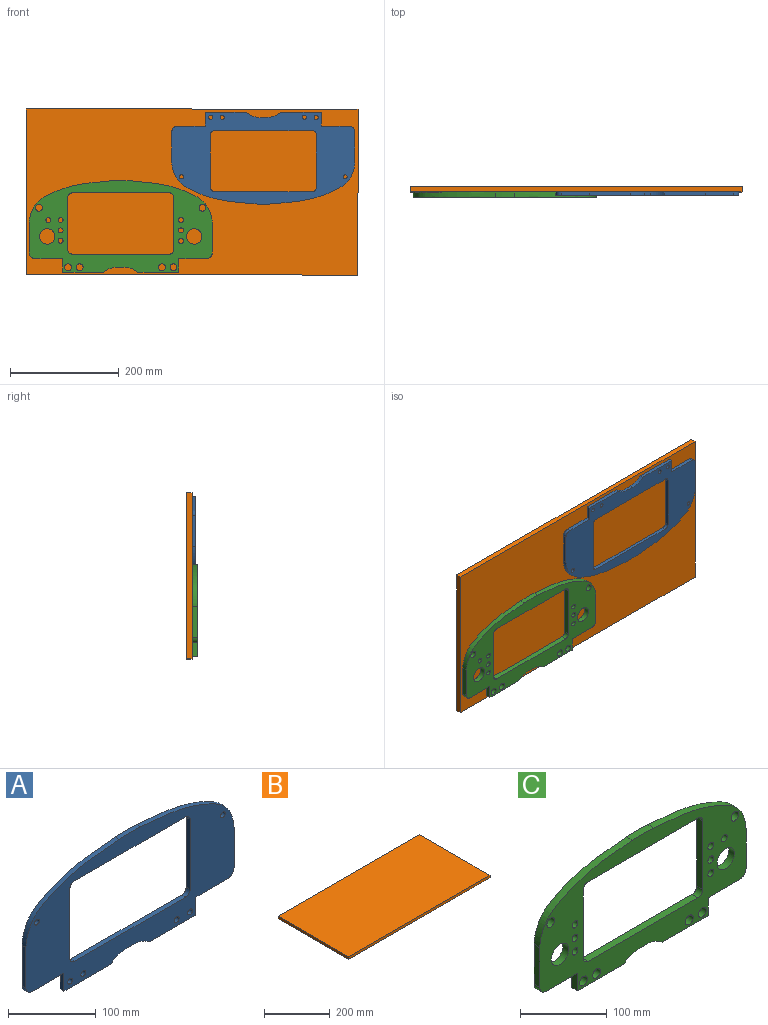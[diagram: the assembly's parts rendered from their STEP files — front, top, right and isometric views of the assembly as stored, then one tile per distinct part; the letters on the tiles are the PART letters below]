
ASSEMBLY  parts=3 mates=3
PART A: 32 faces, bbox 335.9x6.4x168.6 mm
  f0: plane 335.91x168.65mm, normal (0,-1,0), area 25989.5mm2, adj f2,f3,f4,f5,f6,f7,f8,f9
  f1: plane 335.91x168.65mm, normal (0,1,0), area 25989.5mm2, adj f2,f3,f4,f5,f6,f7,f8,f9
  f2: plane 11.66x6.35mm, normal (0,0,-1), area 74.1mm2, adj f0,f1,f3,f20
  f3: cylinder r=39.17mm len=25.6mm, axis (0,1,0), area 177.1mm2, adj f0,f1,f2,f4
  f4: plane 75.09x6.35mm, normal (0,0,-1), area 476.8mm2, adj f0,f1,f3,f5
  f5: plane 25.17x6.35mm, normal (1,0,0), area 159.8mm2, adj f0,f1,f4,f6
  f6: plane 51.28x6.35mm, normal (0,0,-1), area 325.6mm2, adj f0,f1,f5,f21
  f7: plane 56.4x6.35mm, normal (1,0,0), area 358.1mm2, adj f0,f1,f8,f21
  f8: extruded ~150.69x76.24mm, area 1171.7mm2, adj f0,f1,f7,f31
  f9: extruded ~150.69x76.24mm, area 1171.7mm2, adj f0,f1,f10,f31
  f10: plane 56.4x6.35mm, normal (-1,0,0), area 358.1mm2, adj f0,f1,f9,f22
  f11: plane 51.28x6.35mm, normal (0,0,-1), area 325.6mm2, adj f0,f1,f12,f22
  f12: plane 25.17x6.35mm, normal (-1,0,0), area 159.8mm2, adj f0,f1,f11,f13
  f13: plane 75.09x6.35mm, normal (0,0,-1), area 476.8mm2, adj f0,f1,f12,f20
  f14: cylinder r=3.81mm len=7.62mm, axis (0,1,0), area 152mm2, adj f0,f1
  f15: cylinder r=3.81mm len=7.62mm, axis (0,1,0), area 152mm2, adj f0,f1
  f16: cylinder r=3.81mm len=7.62mm, axis (0,1,0), area 152mm2, adj f0,f1
  f17: cylinder r=3.81mm len=7.62mm, axis (0,1,0), area 152mm2, adj f0,f1
  f18: cylinder r=3.81mm len=7.62mm, axis (0,1,0), area 152mm2, adj f0,f1
  f19: cylinder r=3.81mm len=7.62mm, axis (0,1,0), area 152mm2, adj f0,f1
  f20: cylinder r=39.17mm len=25.6mm, axis (0,1,0), area 177.1mm2, adj f0,f1,f2,f13
  f21: cylinder r=10.16mm len=10.16mm, axis (0,1,0), area 101.3mm2, adj f0,f1,f6,f7
  f22: cylinder r=10.16mm len=10.16mm, axis (0,1,0), area 101.3mm2, adj f0,f1,f10,f11
  f23: plane 96.77x6.35mm, normal (-1,0,0), area 614.5mm2, adj f0,f1,f24,f30
  f24: cylinder r=7.77mm len=7.77mm, axis (0,-1,0), area 77.5mm2, adj f0,f1,f23,f25
  f25: plane 178.97x6.35mm, normal (0,0,-1), area 1136.4mm2, adj f0,f1,f24,f26
  f26: cylinder r=7.77mm len=7.77mm, axis (0,-1,0), area 77.5mm2, adj f0,f1,f25,f27
  f27: plane 96.77x6.35mm, normal (1,0,0), area 614.5mm2, adj f0,f1,f26,f28
  f28: cylinder r=7.77mm len=7.77mm, axis (0,-1,0), area 77.5mm2, adj f0,f1,f27,f29
  f29: plane 178.97x6.35mm, normal (0,0,1), area 1136.4mm2, adj f0,f1,f28,f30
  f30: cylinder r=7.77mm len=7.77mm, axis (0,-1,0), area 77.5mm2, adj f0,f1,f23,f29
  f31: cylinder r=254mm len=34.53mm, axis (0,1,0), area 219.4mm2, adj f0,f1,f8,f9
PART B: 6 faces, bbox 609.6x304.8x9.5 mm
  f0: plane 304.8x9.53mm, normal (1,0,0), area 2903.2mm2, adj f1,f3,f4,f5
  f1: plane 609.6x9.53mm, normal (0,1,0), area 5806.4mm2, adj f0,f2,f4,f5
  f2: plane 304.8x9.53mm, normal (-1,0,0), area 2903.2mm2, adj f1,f3,f4,f5
  f3: plane 609.6x9.53mm, normal (0,-1,0), area 5806.4mm2, adj f0,f2,f4,f5
  f4: plane 609.6x304.8mm, normal (0,0,1), area 185806.1mm2, adj f0,f1,f2,f3
  f5: plane 609.6x304.8mm, normal (0,0,-1), area 185806.1mm2, adj f0,f1,f2,f3
PART C: 41 faces, bbox 335.9x9.5x168.6 mm
  f0: plane 335.91x168.65mm, normal (0,-1,0), area 23768.1mm2, adj f2,f3,f4,f5,f6,f7,f8,f9
  f1: plane 335.91x168.65mm, normal (0,1,0), area 23768.1mm2, adj f2,f3,f4,f5,f6,f7,f8,f9
  f2: plane 11.66x9.53mm, normal (0,0,-1), area 111.1mm2, adj f0,f1,f3,f20
  f3: cylinder r=39.17mm len=25.6mm, axis (0,1,0), area 265.7mm2, adj f0,f1,f2,f4
  f4: plane 75.09x9.53mm, normal (0,0,-1), area 715.2mm2, adj f0,f1,f3,f5
  f5: plane 25.17x9.53mm, normal (1,0,0), area 239.8mm2, adj f0,f1,f4,f6
  f6: plane 51.28x9.53mm, normal (0,0,-1), area 488.4mm2, adj f0,f1,f5,f21
  f7: plane 56.4x9.53mm, normal (1,0,0), area 537.2mm2, adj f0,f1,f8,f21
  f8: extruded ~150.69x76.24mm, area 1757.6mm2, adj f0,f1,f7,f31
  f9: extruded ~150.69x76.24mm, area 1757.6mm2, adj f0,f1,f10,f31
  f10: plane 56.4x9.53mm, normal (-1,0,0), area 537.2mm2, adj f0,f1,f9,f22
  f11: plane 51.28x9.53mm, normal (0,0,-1), area 488.4mm2, adj f0,f1,f12,f22
  f12: plane 25.17x9.53mm, normal (-1,0,0), area 239.8mm2, adj f0,f1,f11,f13
  f13: plane 75.09x9.53mm, normal (0,0,-1), area 715.2mm2, adj f0,f1,f12,f20
  f14: cylinder r=6.35mm len=12.7mm, axis (0,1,0), area 380mm2, adj f0,f1
  f15: cylinder r=6.35mm len=12.7mm, axis (0,1,0), area 380mm2, adj f0,f1
  f16: cylinder r=6.35mm len=12.7mm, axis (0,1,0), area 380mm2, adj f0,f1
  f17: cylinder r=6.35mm len=12.7mm, axis (0,1,0), area 380mm2, adj f0,f1
  f18: cylinder r=6.35mm len=12.7mm, axis (0,1,0), area 380mm2, adj f0,f1
  f19: cylinder r=6.35mm len=12.7mm, axis (0,1,0), area 380mm2, adj f0,f1
  f20: cylinder r=39.17mm len=25.6mm, axis (0,1,0), area 265.7mm2, adj f0,f1,f2,f13
  f21: cylinder r=10.16mm len=10.16mm, axis (0,1,0), area 152mm2, adj f0,f1,f6,f7
  f22: cylinder r=10.16mm len=10.16mm, axis (0,1,0), area 152mm2, adj f0,f1,f10,f11
  f23: plane 96.77x9.53mm, normal (-1,0,0), area 921.8mm2, adj f0,f1,f24,f30
  f24: cylinder r=7.77mm len=9.53mm, axis (0,-1,0), area 116.3mm2, adj f0,f1,f23,f25
  f25: plane 178.97x9.53mm, normal (0,0,-1), area 1704.7mm2, adj f0,f1,f24,f26
  f26: cylinder r=7.77mm len=9.53mm, axis (0,-1,0), area 116.3mm2, adj f0,f1,f25,f27
  f27: plane 96.77x9.53mm, normal (1,0,0), area 921.8mm2, adj f0,f1,f26,f28
  f28: cylinder r=7.77mm len=9.53mm, axis (0,-1,0), area 116.3mm2, adj f0,f1,f27,f29
  f29: plane 178.97x9.53mm, normal (0,0,1), area 1704.7mm2, adj f0,f1,f28,f30
  f30: cylinder r=7.77mm len=9.53mm, axis (0,-1,0), area 116.3mm2, adj f0,f1,f23,f29
  f31: cylinder r=254mm len=34.53mm, axis (0,1,0), area 329.1mm2, adj f0,f1,f8,f9
  f32: cylinder r=4.65mm len=9.53mm, axis (0,-1,0), area 278.2mm2, adj f0,f1
  f33: cylinder r=14.16mm len=28.32mm, axis (0,-1,0), area 847.5mm2, adj f0,f1
  f34: cylinder r=4.65mm len=9.53mm, axis (0,-1,0), area 278.2mm2, adj f0,f1
  f35: cylinder r=4.65mm len=9.53mm, axis (0,-1,0), area 278.2mm2, adj f0,f1
  f36: cylinder r=4.65mm len=9.53mm, axis (0,-1,0), area 278.2mm2, adj f0,f1
  f37: cylinder r=4.65mm len=9.53mm, axis (0,-1,0), area 278.2mm2, adj f0,f1
  f38: cylinder r=4.65mm len=9.53mm, axis (0,-1,0), area 278.2mm2, adj f0,f1
  f39: cylinder r=14.16mm len=28.32mm, axis (0,-1,0), area 847.5mm2, adj f0,f1
  f40: cylinder r=4.65mm len=9.53mm, axis (0,-1,0), area 278.2mm2, adj f0,f1
PLACE A rot(axis=(0,-1,0),180deg) t=(238.54,-76.14,109.63)mm
PLACE B rot(axis=(0,-0.71,0.71),180deg) t=(-197.32,-66.61,180.63)mm fixed
PLACE C rot(axis=(0,0,1),180deg) t=(-23.33,-85.66,-54.34)mm
MATE planar B.f4 <-> C.f0  axis (0,-1,0) through (107.48,-76.14,28.23)mm
MATE parallel A.f11 <-> B.f1  axis (0,0,1) through (370.7,-79.31,149.22)mm
MATE planar A.f1 <-> B.f4  axis (0,1,0) through (70.59,-76.14,82.67)mm
